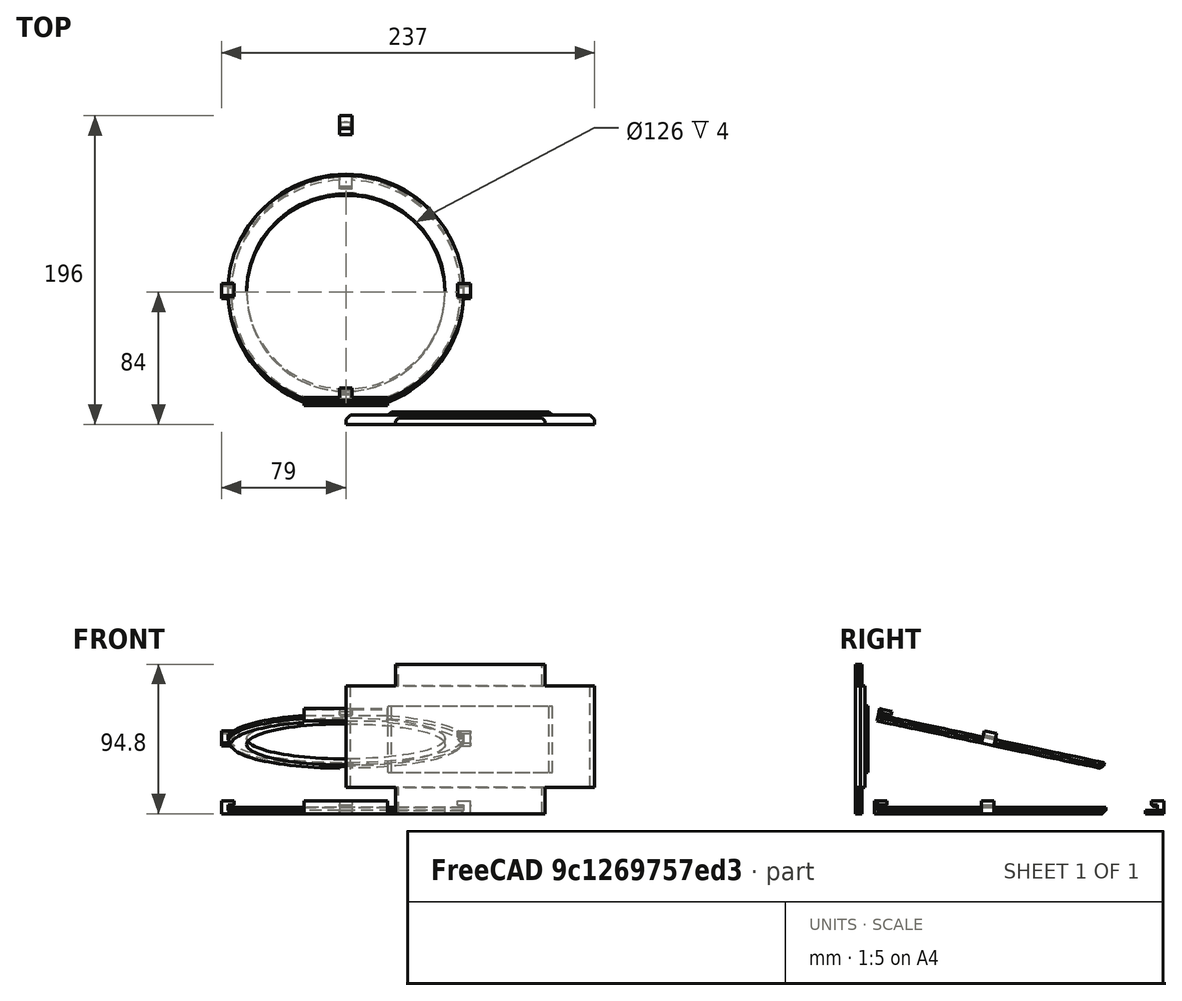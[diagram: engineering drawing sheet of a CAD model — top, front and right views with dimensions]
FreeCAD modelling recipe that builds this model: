
FCSTD DOCUMENT  (FreeCAD 0.19R0.19.2)
Label: waferHolder_011
License: All rights reserved
LicenseURL: http://en.wikipedia.org/wiki/All_rights_reserved
objects: Part::Box×31, Part::Chamfer×28, Part::Cut×10, Sketcher::SketchObject×7, Part::Extrusion×7, Part::MultiFuse×6
note: 89 computed .brp shape members not serialized (recipe doc carries the construction recipe); baked Part::Feature solids carry a one-line shape summary decoded from their .brp

FEATURE [Sketcher::SketchObject] Sketch
  FullyConstrained = true
  sketch-geometry (3):
    g0: Circle CenterX=-3.1415e-12 CenterY=5.6243e-12 CenterZ=0 NormalX=0 NormalY=0 NormalZ=1 AngleXU=0 Radius=63
    g1: ArcOfCircle CenterX=-3.1415e-12 CenterY=5.6243e-12 CenterZ=0 NormalX=0 NormalY=0 NormalZ=1 AngleXU=0 Radius=74.8482 StartAngle=5.07429 EndAngle=10.6337
    g2: LineSegment StartX=-26.5 StartY=-70.0001 StartZ=0 EndX=26.5 EndY=-70.0001 EndZ=0
  constraints (6):
    c: Block(g0)
    c: Coincident(g1,g0)
    c: Block(g1)
    c: Coincident(g2,g1)
    c: Coincident(g2,g1)
    c: Horizontal(g2)
FEATURE [Part::Box] Box  label="holderBitLeft"
  AttacherType = Attacher::AttachEngine3D
  Height = 4
  Length = 8
  Placement = pos=(-79,-4,0) rot=(0,0,1;0rad)
  Width = 8
FEATURE [Part::Box] Box001  label="bitHolderTopCutout"
  AttacherType = Attacher::AttachEngine3D
  Height = 4
  Length = 8
  Placement = pos=(-4,67,-2) rot=(0,0,1;0rad)
  Width = 12
FEATURE [Part::Extrusion] Extrude  label="mainHolderRing"
  Base = -> Sketch
  Dir = (0,0,1)
  DirMode = 2
  FaceMakerClass = Part::FaceMakerBullseye
  LengthFwd = 4
  LengthRev = 0
  Solid = true
  Symmetric = false
FEATURE [Part::Box] Box002  label="holderBitRight"
  AttacherType = Attacher::AttachEngine3D
  Height = 4
  Length = 8
  Placement = pos=(71,-4,0) rot=(0,0,1;0rad)
  Width = 8
FEATURE [Part::Box] Box003  label="bitHolderTop"
  AttacherType = Attacher::AttachEngine3D
  Height = 2
  Length = 8
  Placement = pos=(-4,100,0) rot=(0,0,1;0rad)
  Width = 12
FEATURE [Part::Chamfer] Chamfer
  Base = -> Extrude
  Edges = 1 edges r=2: [Edge3]
FEATURE [Part::Cut] Cut  label="mainHolderRing001"
  Base = -> Chamfer
  Tool = -> Box001
FEATURE [Part::Box] Box004  label="holderBitLeft001"
  AttacherType = Attacher::AttachEngine3D
  Height = 4
  Length = 6
  Placement = pos=(-79,-4,0) rot=(0,0,1;0rad)
  Width = 8
FEATURE [Part::Box] Box005  label="holderBitright002"
  AttacherType = Attacher::AttachEngine3D
  Height = 4
  Length = 6
  Placement = pos=(73,-4,0) rot=(0,0,1;0rad)
  Width = 8
FEATURE [Part::MultiFuse] Fusion  label="holders"
  Shapes = -> [Box004,Box005]
FEATURE [Sketcher::SketchObject] Sketch001
  FullyConstrained = true
  sketch-geometry (3):
    g0: Circle CenterX=-3.1415e-12 CenterY=5.6243e-12 CenterZ=0 NormalX=0 NormalY=0 NormalZ=1 AngleXU=0 Radius=63
    g1: ArcOfCircle CenterX=-3.1415e-12 CenterY=5.6243e-12 CenterZ=0 NormalX=0 NormalY=0 NormalZ=1 AngleXU=0 Radius=74.8482 StartAngle=5.07429 EndAngle=10.6337
    g2: LineSegment StartX=-26.5 StartY=-70.0001 StartZ=0 EndX=26.5 EndY=-70.0001 EndZ=0
  constraints (6):
    c: Block(g0)
    c: Coincident(g1,g0)
    c: Block(g1)
    c: Coincident(g2,g1)
    c: Coincident(g2,g1)
    c: Horizontal(g2)
FEATURE [Part::Extrusion] Extrude001  label="mainHolderRing002"
  Base = -> Sketch001
  Dir = (0,0,1)
  DirMode = 2
  FaceMakerClass = Part::FaceMakerBullseye
  LengthFwd = 4
  LengthRev = 0
  Solid = true
  Symmetric = false
FEATURE [Part::Cut] Cut001  label="leftAndRightHolderBits"
  Base = -> Fusion
  Placement = pos=(0,0,4) rot=(0,0,1;0rad)
  Tool = -> Extrude001
FEATURE [Part::Box] Box006  label="holderBitLeft002"
  AttacherType = Attacher::AttachEngine3D
  Height = 3.4
  Length = 8
  Placement = pos=(-79,-4,4.6) rot=(0,0,1;0rad)
  Width = 8
FEATURE [Part::Box] Box007  label="holderBitRight002"
  AttacherType = Attacher::AttachEngine3D
  Height = 3.4
  Length = 8
  Placement = pos=(71,-4,4.6) rot=(0,0,1;0rad)
  Width = 8
FEATURE [Part::Box] Box008  label="holderBitLeft003"
  AttacherType = Attacher::AttachEngine3D
  Height = 2
  Length = 8
  Placement = pos=(-4,71,2) rot=(0,0,1;0rad)
  Width = 8
FEATURE [Part::Box] Box009  label="bitHolderTopCutout001"
  AttacherType = Attacher::AttachEngine3D
  Height = 4
  Length = 8
  Placement = pos=(-4,67,-2) rot=(0,0,1;0rad)
  Width = 12
FEATURE [Sketcher::SketchObject] Sketch002
  FullyConstrained = true
  sketch-geometry (3):
    g0: Circle CenterX=-3.1415e-12 CenterY=5.6243e-12 CenterZ=0 NormalX=0 NormalY=0 NormalZ=1 AngleXU=0 Radius=63
    g1: ArcOfCircle CenterX=-3.1415e-12 CenterY=5.6243e-12 CenterZ=0 NormalX=0 NormalY=0 NormalZ=1 AngleXU=0 Radius=74.8482 StartAngle=5.07429 EndAngle=10.6337
    g2: LineSegment StartX=-26.5 StartY=-70.0001 StartZ=0 EndX=26.5 EndY=-70.0001 EndZ=0
  constraints (6):
    c: Block(g0)
    c: Coincident(g1,g0)
    c: Block(g1)
    c: Coincident(g2,g1)
    c: Coincident(g2,g1)
    c: Horizontal(g2)
FEATURE [Part::Extrusion] Extrude002  label="mainHolderRing003"
  Base = -> Sketch002
  Dir = (0,0,1)
  DirMode = 2
  FaceMakerClass = Part::FaceMakerBullseye
  LengthFwd = 4
  LengthRev = 0
  Solid = true
  Symmetric = false
FEATURE [Part::Chamfer] Chamfer001
  Base = -> Extrude002
  Edges = 1 edges r=2: [Edge3]
FEATURE [Part::Cut] Cut002  label="mainHolderRing004"
  Base = -> Chamfer001
  Tool = -> Box009
FEATURE [Part::Cut] Cut003  label="bitHolderTop001"
  Base = -> Box008
  Tool = -> Cut002
FEATURE [Part::Box] Box010  label="holderBitLeft004"
  AttacherType = Attacher::AttachEngine3D
  Height = 2
  Length = 8
  Placement = pos=(-4,71,2) rot=(0,0,1;0rad)
  Width = 8
FEATURE [Part::Box] Box011  label="bitHolderTopCutout002"
  AttacherType = Attacher::AttachEngine3D
  Height = 4
  Length = 8
  Placement = pos=(-4,67,-2) rot=(0,0,1;0rad)
  Width = 12
FEATURE [Sketcher::SketchObject] Sketch003
  FullyConstrained = true
  sketch-geometry (3):
    g0: Circle CenterX=-3.1415e-12 CenterY=5.6243e-12 CenterZ=0 NormalX=0 NormalY=0 NormalZ=1 AngleXU=0 Radius=63
    g1: ArcOfCircle CenterX=-3.1415e-12 CenterY=5.6243e-12 CenterZ=0 NormalX=0 NormalY=0 NormalZ=1 AngleXU=0 Radius=74.8482 StartAngle=5.07429 EndAngle=10.6337
    g2: LineSegment StartX=-26.5 StartY=-70.0001 StartZ=0 EndX=26.5 EndY=-70.0001 EndZ=0
  constraints (6):
    c: Block(g0)
    c: Coincident(g1,g0)
    c: Block(g1)
    c: Coincident(g2,g1)
    c: Coincident(g2,g1)
    c: Horizontal(g2)
FEATURE [Part::Extrusion] Extrude003  label="mainHolderRing006"
  Base = -> Sketch003
  Dir = (0,0,1)
  DirMode = 2
  FaceMakerClass = Part::FaceMakerBullseye
  LengthFwd = 4
  LengthRev = 0
  Solid = true
  Symmetric = false
FEATURE [Part::Chamfer] Chamfer002
  Base = -> Extrude003
  Edges = 1 edges r=2: [Edge3]
FEATURE [Part::Cut] Cut005  label="mainHolderRing005"
  Base = -> Chamfer002
  Tool = -> Box011
FEATURE [Part::Cut] Cut004  label="bitHolderTop002"
  Base = -> Box010
  Placement = pos=(0,0,2) rot=(0,0,1;0rad)
  Tool = -> Cut005
FEATURE [Part::Box] Box012  label="holderBitLeft005"
  AttacherType = Attacher::AttachEngine3D
  Height = 2
  Length = 8
  Placement = pos=(-4,71,2) rot=(0,0,1;0rad)
  Width = 8
FEATURE [Part::Box] Box013  label="bitHolderTopCutout003"
  AttacherType = Attacher::AttachEngine3D
  Height = 4
  Length = 8
  Placement = pos=(-4,67,-2) rot=(0,0,1;0rad)
  Width = 12
FEATURE [Sketcher::SketchObject] Sketch004
  FullyConstrained = true
  sketch-geometry (3):
    g0: Circle CenterX=-3.1415e-12 CenterY=5.6243e-12 CenterZ=0 NormalX=0 NormalY=0 NormalZ=1 AngleXU=0 Radius=63
    g1: ArcOfCircle CenterX=-3.1415e-12 CenterY=5.6243e-12 CenterZ=0 NormalX=0 NormalY=0 NormalZ=1 AngleXU=0 Radius=74.8482 StartAngle=5.07429 EndAngle=10.6337
    g2: LineSegment StartX=-26.5 StartY=-70.0001 StartZ=0 EndX=26.5 EndY=-70.0001 EndZ=0
  constraints (6):
    c: Block(g0)
    c: Coincident(g1,g0)
    c: Block(g1)
    c: Coincident(g2,g1)
    c: Coincident(g2,g1)
    c: Horizontal(g2)
FEATURE [Part::Extrusion] Extrude004  label="mainHolderRing008"
  Base = -> Sketch004
  Dir = (0,0,1)
  DirMode = 2
  FaceMakerClass = Part::FaceMakerBullseye
  LengthFwd = 4
  LengthRev = 0
  Solid = true
  Symmetric = false
FEATURE [Part::Chamfer] Chamfer003
  Base = -> Extrude004
  Edges = 1 edges r=2: [Edge3]
FEATURE [Part::Cut] Cut007  label="mainHolderRing007"
  Base = -> Chamfer003
  Tool = -> Box013
FEATURE [Part::Cut] Cut006  label="bitHolderTop003"
  Base = -> Box012
  Placement = pos=(0,0,4) rot=(0,0,1;0rad)
  Tool = -> Cut007
FEATURE [Part::Box] Box014  label="bitHoldertop006"
  AttacherType = Attacher::AttachEngine3D
  Height = 3.4
  Length = 8
  Placement = pos=(-4,71,4.6) rot=(0,0,1;0rad)
  Width = 8
FEATURE [Part::MultiFuse] Fusion001  label="holderTop"
  Placement = pos=(0,33,0) rot=(0,0,1;0rad)
  Shapes = -> [Cut003,Cut004,Cut006,Box014]
FEATURE [Part::Chamfer] Chamfer004
  Base = -> Fusion001
  Edges = 1 edges r=1: [Edge16]
FEATURE [Part::Chamfer] Chamfer005
  Base = -> Box006
  Edges = 1 edges r=1: [Edge8]
FEATURE [Part::Chamfer] Chamfer006
  Base = -> Box007
  Edges = 1 edges r=1: [Edge4]
FEATURE [Part::Chamfer] Chamfer007
  Base = -> Chamfer006
  Edges = 1 edges r=1: [Edge13]
FEATURE [Part::Chamfer] Chamfer008
  Base = -> Chamfer007
  Edges = 1 edges r=1: [Edge5]
FEATURE [Part::Chamfer] Chamfer009
  Base = -> Chamfer004
  Edges = 1 edges r=1: [Edge1]
FEATURE [Part::Chamfer] Chamfer010
  Base = -> Chamfer009
  Edges = 1 edges r=1: [Edge32]
FEATURE [Part::Chamfer] Chamfer011
  Base = -> Chamfer005
  Edges = 1 edges r=1: [Edge5]
FEATURE [Part::Chamfer] Chamfer012
  Base = -> Chamfer011
  Edges = 1 edges r=1: [Edge16]
FEATURE [Part::Box] Box015  label="holderBottom"
  AttacherType = Attacher::AttachEngine3D
  Height = 4
  Length = 53
  Placement = pos=(-26.5,-72,0) rot=(0,0,1;0rad)
  Width = 4.5
FEATURE [Part::Box] Box016  label="holderBottom001"
  AttacherType = Attacher::AttachEngine3D
  Height = 4
  Length = 53
  Placement = pos=(-26.5,-72,4) rot=(0,0,1;0rad)
  Width = 2
FEATURE [Part::Box] Box017  label="holderBottom002"
  AttacherType = Attacher::AttachEngine3D
  Height = 3.4
  Length = 8
  Placement = pos=(-4,-72,4.6) rot=(0,0,1;0rad)
  Width = 8
FEATURE [Part::Chamfer] Chamfer013  label="holderBottom003"
  Base = -> Box017
  Edges = 3 edges r=1: [Edge4,Edge8,Edge11]
FEATURE [Part::Box] Box018  label="base001"
  AttacherType = Attacher::AttachEngine3D
  Height = 64.44
  Length = 158
  Placement = pos=(0,-84,16.6) rot=(0,0,1;0rad)
  Width = 6
FEATURE [Part::Box] Box019  label="base002"
  AttacherType = Attacher::AttachEngine3D
  Height = 94.8
  Length = 94.8
  Placement = pos=(31.6,-84,0) rot=(0,0,1;0rad)
  Width = 4
FEATURE [Part::Box] Box020  label="base003"
  AttacherType = Attacher::AttachEngine3D
  Height = 42.44
  Length = 104.28
  Placement = pos=(26.86,-84,26.18) rot=(0,0,1;0rad)
  Width = 8
FEATURE [Part::Chamfer] Chamfer014
  Base = -> Box018
  Edges = 1 edges r=3: [Edge3]
FEATURE [Part::Chamfer] Chamfer015
  Base = -> Chamfer014
  Edges = 1 edges r=3: [Edge15]
FEATURE [Part::Chamfer] Chamfer016
  Base = -> Box019
  Edges = 1 edges r=2: [Edge3]
FEATURE [Part::Chamfer] Chamfer017
  Base = -> Box020
  Edges = 1 edges r=2: [Edge3]
FEATURE [Part::Chamfer] Chamfer018
  Base = -> Chamfer016
  Edges = 1 edges r=2: [Edge15]
FEATURE [Part::Chamfer] Chamfer019
  Base = -> Chamfer017
  Edges = 1 edges r=2: [Edge15]
FEATURE [Part::MultiFuse] Fusion002  label="base004"
  Shapes = -> [Chamfer015,Chamfer018,Chamfer019]
FEATURE [Part::MultiFuse] Fusion003  label="ringHolder"
  Shapes = -> [Box,Box002,Cut,Cut001,Chamfer008,Chamfer012,Box015,Box016,Chamfer013]
FEATURE [Part::Box] Box021  label="holderBitLeft006"
  AttacherType = Attacher::AttachEngine3D
  Height = 4
  Length = 6
  Placement = pos=(-79,-4,0) rot=(0,0,1;0rad)
  Width = 8
FEATURE [Part::Box] Box022  label="holderBitright003"
  AttacherType = Attacher::AttachEngine3D
  Height = 4
  Length = 6
  Placement = pos=(73,-4,0) rot=(0,0,1;0rad)
  Width = 8
FEATURE [Part::Box] Box023  label="holderBitLeft007"
  AttacherType = Attacher::AttachEngine3D
  Height = 3.4
  Length = 8
  Placement = pos=(-79,-4,4.6) rot=(0,0,1;0rad)
  Width = 8
FEATURE [Part::Box] Box024  label="holderBitRight003"
  AttacherType = Attacher::AttachEngine3D
  Height = 3.4
  Length = 8
  Placement = pos=(71,-4,4.6) rot=(0,0,1;0rad)
  Width = 8
FEATURE [Sketcher::SketchObject] Sketch005
  FullyConstrained = true
  sketch-geometry (3):
    g0: Circle CenterX=-3.1415e-12 CenterY=5.6243e-12 CenterZ=0 NormalX=0 NormalY=0 NormalZ=1 AngleXU=0 Radius=63
    g1: ArcOfCircle CenterX=-3.1415e-12 CenterY=5.6243e-12 CenterZ=0 NormalX=0 NormalY=0 NormalZ=1 AngleXU=0 Radius=74.8482 StartAngle=5.07429 EndAngle=10.6337
    g2: LineSegment StartX=-26.5 StartY=-70.0001 StartZ=0 EndX=26.5 EndY=-70.0001 EndZ=0
  constraints (6):
    c: Block(g0)
    c: Coincident(g1,g0)
    c: Block(g1)
    c: Coincident(g2,g1)
    c: Coincident(g2,g1)
    c: Horizontal(g2)
FEATURE [Part::Box] Box025  label="holderBitLeft008"
  AttacherType = Attacher::AttachEngine3D
  Height = 4
  Length = 8
  Placement = pos=(-79,-4,0) rot=(0,0,1;0rad)
  Width = 8
FEATURE [Part::Box] Box026  label="bitHolderTopCutout004"
  AttacherType = Attacher::AttachEngine3D
  Height = 4
  Length = 8
  Placement = pos=(-4,67,-2) rot=(0,0,1;0rad)
  Width = 12
FEATURE [Part::Extrusion] Extrude006  label="mainHolderRing010"
  Base = -> Sketch005
  Dir = (0,0,1)
  DirMode = 2
  FaceMakerClass = Part::FaceMakerBullseye
  LengthFwd = 4
  LengthRev = 0
  Solid = true
  Symmetric = false
FEATURE [Part::Box] Box027  label="holderBitRight004"
  AttacherType = Attacher::AttachEngine3D
  Height = 4
  Length = 8
  Placement = pos=(71,-4,0) rot=(0,0,1;0rad)
  Width = 8
FEATURE [Part::Chamfer] Chamfer020
  Base = -> Extrude006
  Edges = 1 edges r=2: [Edge3]
FEATURE [Part::Cut] Cut008  label="mainHolderRing011"
  Base = -> Chamfer020
  Tool = -> Box026
FEATURE [Part::MultiFuse] Fusion004  label="holders001"
  Shapes = -> [Box021,Box022]
FEATURE [Sketcher::SketchObject] Sketch006
  FullyConstrained = true
  sketch-geometry (3):
    g0: Circle CenterX=-3.1415e-12 CenterY=5.6243e-12 CenterZ=0 NormalX=0 NormalY=0 NormalZ=1 AngleXU=0 Radius=63
    g1: ArcOfCircle CenterX=-3.1415e-12 CenterY=5.6243e-12 CenterZ=0 NormalX=0 NormalY=0 NormalZ=1 AngleXU=0 Radius=74.8482 StartAngle=5.07429 EndAngle=10.6337
    g2: LineSegment StartX=-26.5 StartY=-70.0001 StartZ=0 EndX=26.5 EndY=-70.0001 EndZ=0
  constraints (6):
    c: Block(g0)
    c: Coincident(g1,g0)
    c: Block(g1)
    c: Coincident(g2,g1)
    c: Coincident(g2,g1)
    c: Horizontal(g2)
FEATURE [Part::Extrusion] Extrude005  label="mainHolderRing009"
  Base = -> Sketch006
  Dir = (0,0,1)
  DirMode = 2
  FaceMakerClass = Part::FaceMakerBullseye
  LengthFwd = 4
  LengthRev = 0
  Solid = true
  Symmetric = false
FEATURE [Part::Cut] Cut009  label="leftAndRightHolderBits001"
  Base = -> Fusion004
  Placement = pos=(0,0,4) rot=(0,0,1;0rad)
  Tool = -> Extrude005
FEATURE [Part::Chamfer] Chamfer021
  Base = -> Box023
  Edges = 1 edges r=1: [Edge8]
FEATURE [Part::Chamfer] Chamfer022
  Base = -> Box024
  Edges = 1 edges r=1: [Edge4]
FEATURE [Part::Chamfer] Chamfer023
  Base = -> Chamfer022
  Edges = 1 edges r=1: [Edge13]
FEATURE [Part::Chamfer] Chamfer024
  Base = -> Chamfer023
  Edges = 1 edges r=1: [Edge5]
FEATURE [Part::Box] Box028  label="holderBottom004"
  AttacherType = Attacher::AttachEngine3D
  Height = 4
  Length = 53
  Placement = pos=(-26.5,-72,0) rot=(0,0,1;0rad)
  Width = 4.5
FEATURE [Part::Chamfer] Chamfer025
  Base = -> Chamfer021
  Edges = 1 edges r=1: [Edge5]
FEATURE [Part::Chamfer] Chamfer026
  Base = -> Chamfer025
  Edges = 1 edges r=1: [Edge16]
FEATURE [Part::Box] Box029  label="holderBottom006"
  AttacherType = Attacher::AttachEngine3D
  Height = 4
  Length = 53
  Placement = pos=(-26.5,-72,4) rot=(0,0,1;0rad)
  Width = 2
FEATURE [Part::Box] Box030  label="holderBottom007"
  AttacherType = Attacher::AttachEngine3D
  Height = 3.4
  Length = 8
  Placement = pos=(-4,-72,4.6) rot=(0,0,1;0rad)
  Width = 8
FEATURE [Part::Chamfer] Chamfer027  label="holderBottom005"
  Base = -> Box030
  Edges = 3 edges r=1: [Edge4,Edge8,Edge11]
FEATURE [Part::MultiFuse] Fusion005  label="ringHolder001"
  Placement = pos=(0,0,44) rot=(1,0,0;6.07375rad)
  Shapes = -> [Box025,Box027,Cut008,Cut009,Chamfer024,Chamfer026,Box028,Box029,Chamfer027]
